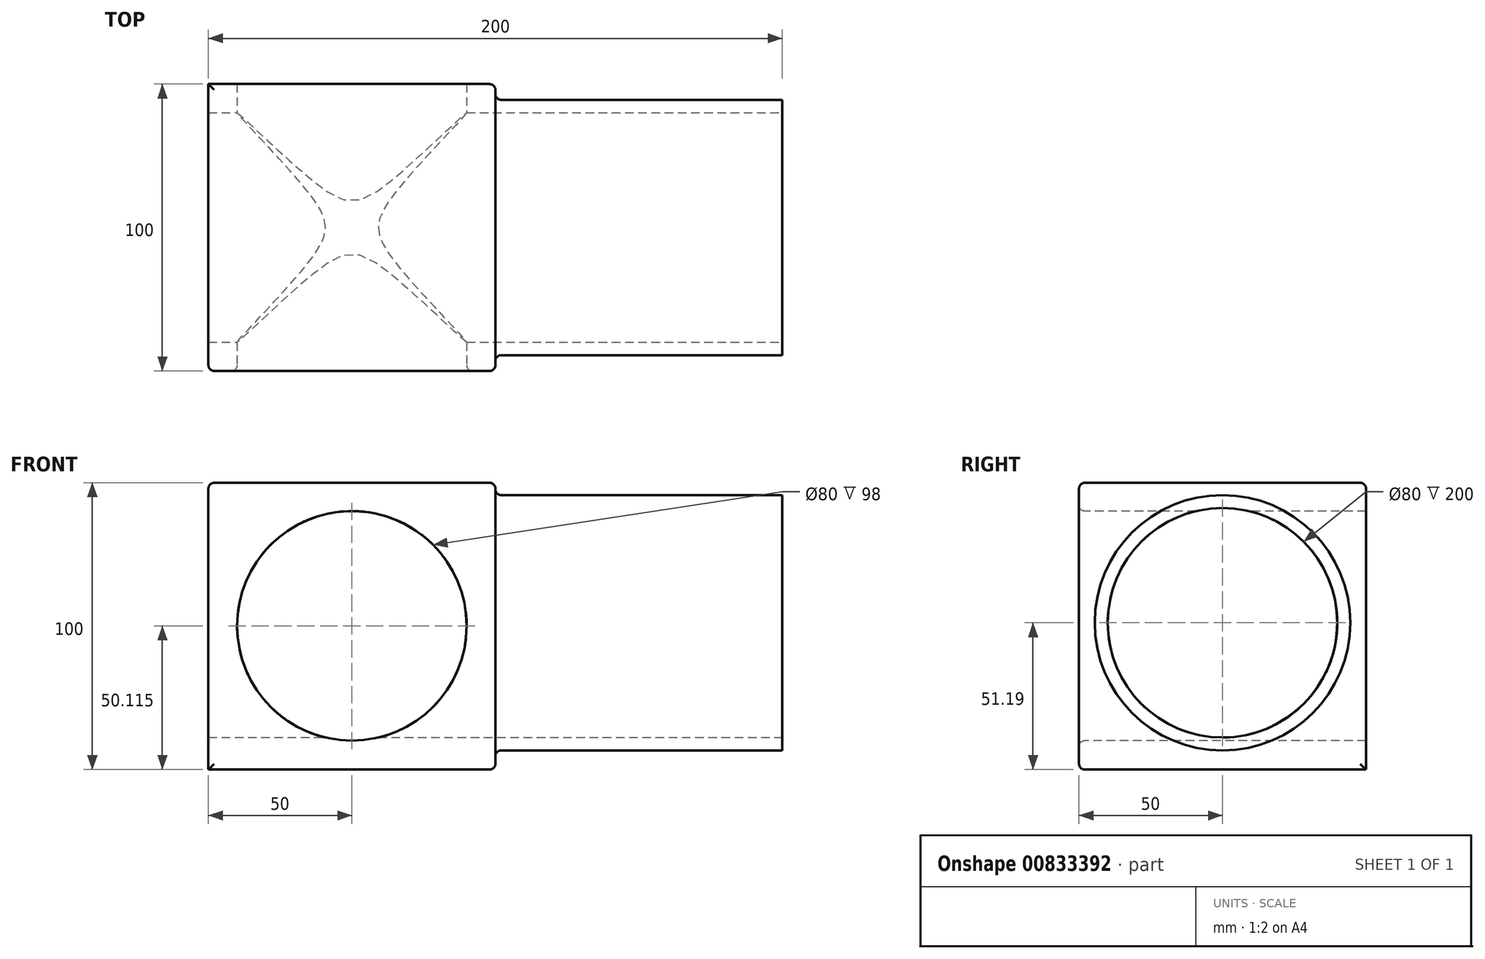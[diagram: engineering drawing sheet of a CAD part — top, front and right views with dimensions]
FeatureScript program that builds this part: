
annotation { "Feature Type Name" : "Feature", "Feature Type Description" : "" }
export const myFeature = defineFeature(function(context is Context, id is Id, definition is map)
    precondition{}
    {
        {
            var Q0;
            Q0=qCreatedBy(makeId("Top.planeOp"),FACE);
            var sketch = newSketch(context, id + "F0", { "sketchPlane" : qUnion([Q0])});
            skLineSegment(sketch, "E0.bottom", {"start": v(50, -50) * mm, "end": v(-50, -50) * mm});
            skLineSegment(sketch, "E0.top", {"start": v(50, 50) * mm, "end": v(-50, 50) * mm});
            skLineSegment(sketch, "E0.left", {"start": v(50, -50) * mm, "end": v(50, 50) * mm});
            skLineSegment(sketch, "E0.right", {"start": v(-50, -50) * mm, "end": v(-50, 50) * mm});
            skPoint(sketch, "E0.middle", {"position": v(0, 0) * mm});
            skSolve(sketch);
        }
        {
            var Q0;
            Q0 = qSketchRegion(id + "F0", true);
            extrude(context, id + "F1", {"entities" : qUnion([Q0]), "depth" : 100 * mm, "offsetDistance" : 25 * mm});
        }
        {
            var Q0;
            Q0=makeQuery(id+"F1.opExtrude","SWEPT_FACE",FACE,{"disambiguationData":[OSD([sQuery(id+"F0.wireOp",EDGE,"E0.left")])]});
            var sketch = newSketch(context, id + "F2", { "sketchPlane" : qUnion([Q0])});
            skCircle(sketch, "E1", {"center": v(0, 51.19) * mm, "radius": 40 * mm});
            skCircle(sketch, "E2", {"center": v(0, 51.19) * mm, "radius": 44.52 * mm});
            skSolve(sketch);
        }
        {
            var Q0;
            Q0=makeQuery(id+"F2.imprint","IMPRINT",FACE,{"disambiguationData":[TD([[makeQuery(id+"F2.imprint","IMPRINT",EDGE,{"derivedFrom":sQuery(id+"F2.wireOp",EDGE,"E1")}),1.0]])]});
            extrude(context, id + "F3", {"entities" : qUnion([Q0]), "operationType" : NewBodyOperationType.REMOVE, "endBound" : BoundingType.THROUGH_ALL, "oppositeDirection" : true, "depth" : 25 * mm, "offsetDistance" : 25 * mm});
        }
        {
            var Q0;
            Q0=makeQuery(id+"F1.opExtrude","SWEPT_FACE",FACE,{"disambiguationData":[OSD([sQuery(id+"F0.wireOp",EDGE,"E0.bottom")])]});
            var sketch = newSketch(context, id + "F4", { "sketchPlane" : qUnion([Q0])});
            skCircle(sketch, "E3", {"center": v(0, 50.11) * mm, "radius": 40 * mm});
            skSolve(sketch);
        }
        {
            var Q0;
            Q0=makeQuery(id+"F4.imprint","IMPRINT",FACE,{"disambiguationData":[TD([[makeQuery(id+"F4.imprint","IMPRINT",EDGE,{"derivedFrom":sQuery(id+"F4.wireOp",EDGE,"E3")}),1.0]])]});
            var Q1;
            Q1=sQuery(id+"F4.wireOp",EDGE,"E3");
            extrude(context, id + "F5", {"entities" : qUnion([Q0]), "operationType" : NewBodyOperationType.REMOVE, "surfaceEntities" : qUnion([Q1]), "endBound" : BoundingType.THROUGH_ALL, "oppositeDirection" : true, "depth" : 25 * mm, "offsetDistance" : 25 * mm});
        }
        {
            var Q0;
            Q0=makeQuery(id+"F2.imprint","IMPRINT",FACE,{"disambiguationData":[TD([[makeQuery(id+"F2.imprint","IMPRINT",EDGE,{"derivedFrom":sQuery(id+"F2.wireOp",EDGE,"E1")}),-1.0]])]});
            var Q1;
            Q1=sQuery(id+"F2.wireOp",EDGE,"E2");
            extrude(context, id + "F6", {"entities" : qUnion([Q0]), "operationType" : NewBodyOperationType.ADD, "surfaceEntities" : qUnion([Q1]), "depth" : 100 * mm, "offsetDistance" : 25 * mm});
        }
        {
            var Q0;
            Q0=makeQuery(id+"F1.opExtrude","CAP_FACE",FACE,{"disambiguationData":[OSD([sQuery(id+"F0.wireOp",EDGE,"E0.bottom"),sQuery(id+"F0.wireOp",EDGE,"E0.top"),sQuery(id+"F0.wireOp",EDGE,"E0.left"),sQuery(id+"F0.wireOp",EDGE,"E0.right")])],"isStart":false});
            var Q1;
            Q1=makeQuery(id+"F1.opExtrude","SWEPT_FACE",FACE,{"disambiguationData":[OSD([sQuery(id+"F0.wireOp",EDGE,"E0.left")])]});
            var Q2;
            Q2=makeQuery(id+"F1.opExtrude","SWEPT_FACE",FACE,{"disambiguationData":[OSD([sQuery(id+"F0.wireOp",EDGE,"E0.bottom")])]});
            fillet(context, id + "F7", {"entities" : qUnion([Q0, Q1, Q2]), "radius" : 2 * mm, "tangentPropagation" : true, "allowEdgeOverflow" : false});
        }
    });
